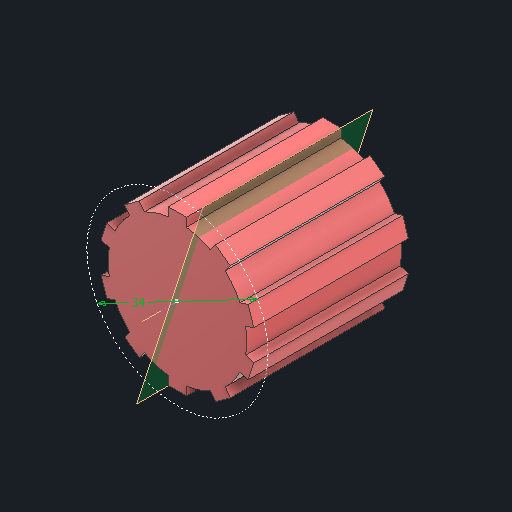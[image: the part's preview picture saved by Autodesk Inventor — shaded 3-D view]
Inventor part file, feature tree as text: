
AUTODESK INVENTOR PART (.ipt)
format: ipt  version: 2024 (Build 280153000, 153)  size: 245,760 bytes
history: native  units: in
note: dims shown in document units (in); Inventor stores cm internally (conversion verified against a paired STEP export)
features: sketch x5, extrude x3, plane x2, projected_geometry x1
ambient origin geometry x8: Origin, YZ Plane, XZ Plane, XY Plane, X Axis, Y Axis, Z Axis, Center Point
bodies: Solid1 (feature_tree)
feature tree (11):
  extrude  "Extrusion1"  Depth=3.937in TaperAngle=360.0deg
  extrude  "Extrusion2"  Depth=0.4331in TaperAngle=0.0deg
  extrude  "Extrusion3"  Depth=0.3543in TaperAngle=0.0deg
  plane  "Work Plane1"
  sketch  "Sketch4"  dims[d14=0.2362in]
  plane  "Work Plane2"
  sketch  "Sketch5"  dims[d15=0.5118in d16=1.3386in d17=0.6693in d18=0.0in d19=1.3386in]
  sketch  "Sketch1"  dims[d1=1.1811in d3=3.937in d5=360.0deg]
  sketch  "Sketch2"  dims[d7=1.1417in d8=0.0in d9=0.4331in d10=0.0in]
  projected_geometry  "Projected Loop1"
  sketch  "Sketch3"  dims[d11=0.1969in d12=0.3543in d13=0.0in]
